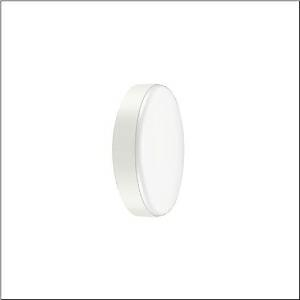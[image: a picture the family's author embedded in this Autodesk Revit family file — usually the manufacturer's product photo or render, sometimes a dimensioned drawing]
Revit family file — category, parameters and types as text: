
# Revit family: round_31_51wc10da32as
name_source: partatom
category: Lighting Fixtures
units: mm (PartAtom-declared; Revit-internal decimal feet)

## family parameters
Cut with Voids When Loaded = No
Host = Face
Light Source = No
Part Type = Normal
Room Calculation Point = No
Round Connector Dimension = Use Diameter
Shared = No

## types (1)
- Round 31 (1 x LED, 2450 lm, 20.4 W, 3000K)
    Apparent Load = 20 VA
    CIE Flux Codes = 44 75 94 94 100
    Color Rendering = 80
    Color Temperature = 3000K
    Default Elevation = 1800 mm
    Description = Round 31, wall and ceiling luminaire, primary optical cover: cover, of PC, opal, light emission: direct distribution, primary light characteristic: symmetric, installation type: surface-mounted, LED, rated luminous flux: 2.450lm, luminous efficacy: 120lm/W, light colour: 830, colour temperature: 3000K, control gear: DALI 2, with terminal, 5-pole, max. 2.5mm², mains connection: 220..240V, AC, 50/60Hz, rated input power: 20.5W, luminaire housing, of PC, traffic white (RAL 9016), diameter: 350mm, brightness and presence sensor, HF sensor, protection rating (complete): IP65, insulation class (complete): insulation class II (safety insulation), certification: CE, impact resistance: IK10, permissible operating ambient temperature: -20..+40°C, permissible storage temperature: -20..+60°C, packaging unit: 1 piece
    Height = 97 mm
    Lamp = 1 x LED
    Lamp Light Flux = 2450 lm
    Lamp Power = 20.4 W
    Lamp count = 1
    Length = 350 mm
    Luminous efficacy = 120 lm/W
    Manufacturer = Siteco
    ModVariant = No
    Model = 51WC10DA32AS
    Mounting Place = Wall
    Mounting Type = Surface mounted
    Number of Poles = 1
    OnlyDefault = Yes
    Power Factor = 1
    Product Name = Round 31
    Product group = wall and ceiling luminaire | wall mounted
    ProductGroupID = 2001
    Protection Class = Protection class II
    Protection Degree = IP 65
    RLX_Detail_Level = 1
    RLX_Emergency_Light_Flux = 0 lm
    RLX_Emergency_Type = 0
    RLX_Emergency_Type_DB = No
    RlxData = <blob elided: 29801 chars, md5=9a94de05>
    Socket = socket
    Standby Power = 0 W
    System Light Flux = 2450 lm
    System Power = 20 W
    Type Comments = Product without accessories
    Type Image = l_1007027.jpg
    URL = http://relux.com
    VarID = ---
    Voltage = 0 V
    Weight = 0.00 kg
    Width = 0 mm  [stored 0 ft]

note: [stored X ft] marks values corroborated as IEEE doubles in the binary element streams (Revit-internal decimal feet)

## geometry (parser evidence)
native form markers: Blend x4, Sweep x12
no freeform markers — native parametric forms only
